# Revit family: Hager-Vision-IP30-syst-NoHosted-NL-en
name_source: partatom
category: Electrical Equipment
units: mm (PartAtom-declared; Revit-internal decimal feet)

## family parameters
Always vertical = Yes
Cut with Voids When Loaded = No
Panel Configuration = Two Columns, Circuits Across
Part Type = Panelboard
Room Calculation Point = No
Round Connector Dimension = Use Diameter
Shared = No
Work Plane-Based = Yes

## types (5) — shared parameters
Default Elevation = 1219 mm
EF000003 - Mounting method = EV000384 - Surface mounted (plaster)
EF000007 - Colour = EV000270 - Grey
EF000008 - Width = 220 mm  [stored 0.721785 ft]
EF000049 - Depth = 89 mm  [stored 0.291995 ft]
EF000116 - RAL-number = 7035
EF000118 - With mounting plate = No
EF000339 - Type of cover = EV001012 - Cover
EF001062 - EMC-version = No
EF001088 - Extension possible = Yes
EF001131 - Internal depth = 80 mm
EF001134 - DIN-rail = No
EF001596 - Material housing = EV000139 - Plastic
EF002950 - Width in number of modular spacings = 12
EF004462 - Type of closure = EV000154 - Other
EF005474 - Degree of protection (IP) = EV006410 - IP30
EF006244 - Transparent cover/door = No
EF006306 - With lock = No
EF009212 - Cover model = EV000116 - Closed
EF015776 - Earthing terminal block = No
EF015777 - Neutral terminal block = No
EF015941 - Signal passing door = No
HG000001 - Number of columns = 1
HG000002 - With door or cover = Yes
HG000003 - Range = Vision
HG000005 - Thickness = 3 mm  [stored 0.00984252 ft]
HG000006 - Flush mounted = No
HG000009 - Double swing door = No
HG000010 - Asymmetric doors = No
HG000011 - Empty rows from bottom = No
HG000017 - Distance between poles = 18 mm  [stored 0.0590551 ft]
Manufacturer = Hager
Type Comments = Vision
zero-valued in all types: EF000218 - Built-in depth, EF000332 - Built-in height, EF000846 - Built-in width, HG000007 - Number of empty columns, HG000008 - Number of empty rows

## per-type parameters (varying)
| type | EF000040 - Height | EF000266 - Number of rows | HG000004 - Manufacturer reference | Model |
| Surface mounted IP30 W220 H220 D89 12 Modular spacings - VKG21Z | 220 mm  [stored 0.721785 ft] | 1 | VKG21Z | VKG21Z |
| Surface mounted IP30 W220 H330 D89 12 Modular spacings - VKG22Z | 330 mm | 2 | VKG22Z | VKG22Z |
| Surface mounted IP30 W220 H365 D89 12 Modular spacings - VKG21S | 365 mm | 1 | VKG21S | VKG21S |
| Surface mounted IP30 W220 H475 D89 12 Modular spacings - VKG22S | 475 mm  [stored 1.5584 ft] | 2 | VKG22S | VKG22S |
| Surface mounted IP30 W220 H695 D89 12 Modular spacings - VKG23S | 695 mm  [stored 2.28018 ft] | 3 | VKG23S | VKG23S |

note: [stored X ft] marks values corroborated as IEEE doubles in the binary element streams (Revit-internal decimal feet)

## geometry (parser evidence)
native form markers: Sweep x14
no freeform markers — native parametric forms only
